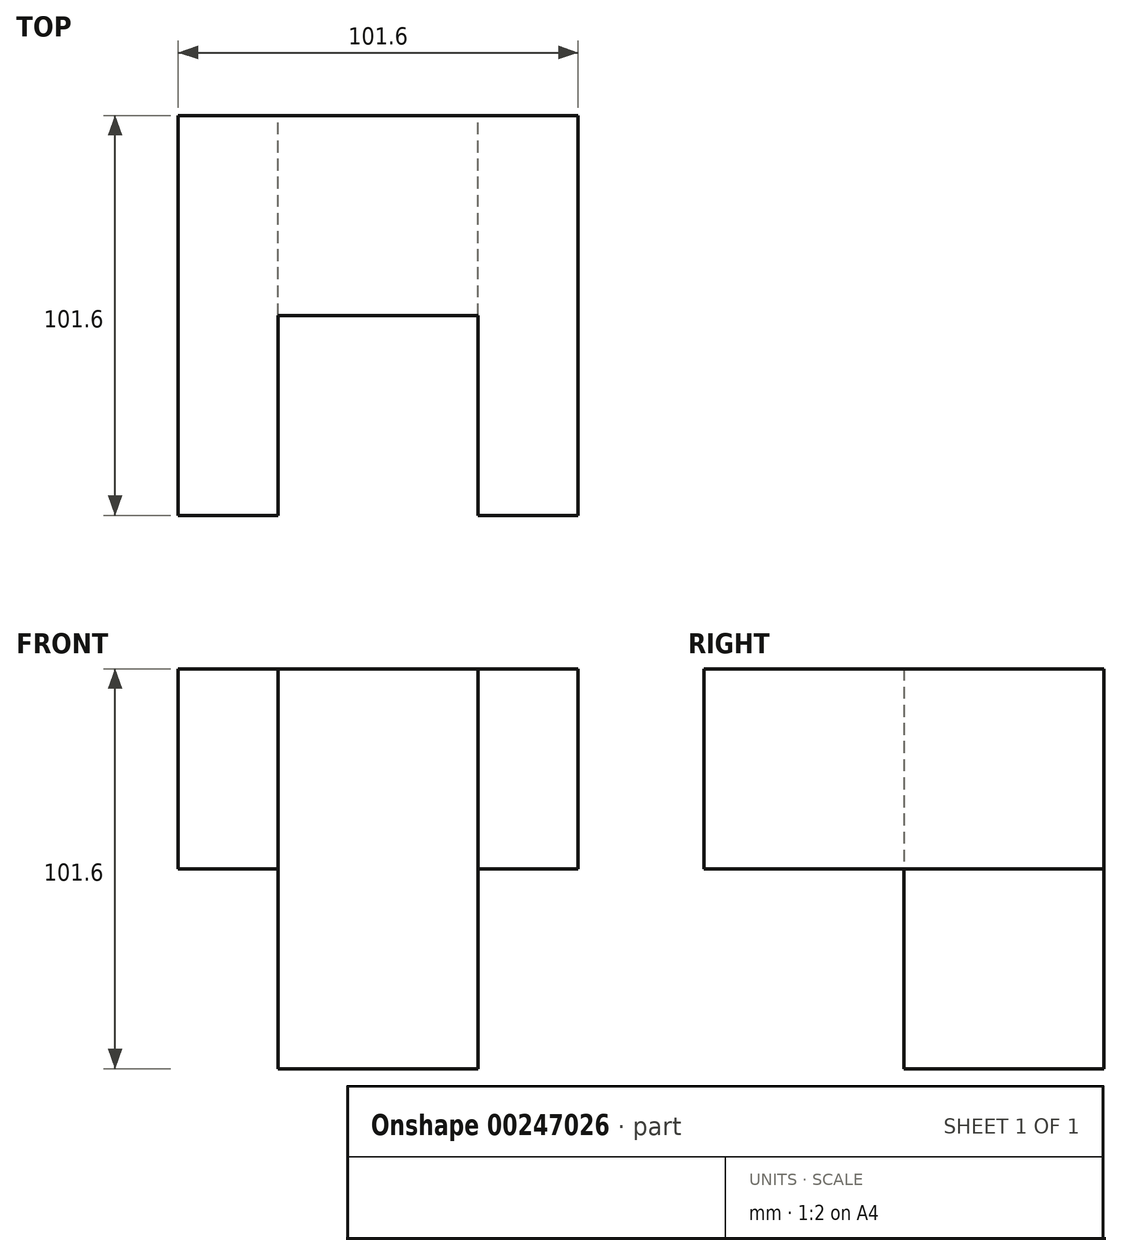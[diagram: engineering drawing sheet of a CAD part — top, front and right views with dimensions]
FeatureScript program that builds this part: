
annotation { "Feature Type Name" : "Feature", "Feature Type Description" : "" }
export const myFeature = defineFeature(function(context is Context, id is Id, definition is map)
    precondition{}
    {
        {
            var Q0;
            Q0=qCreatedBy(makeId("Front.planeOp"),FACE);
            var sketch = newSketch(context, id + "F0", { "sketchPlane" : qUnion([Q0])});
            skLineSegment(sketch, "E0.bottom", {"start": v(-58.42, 78.35) * mm, "end": v(43.18, 78.35) * mm});
            skLineSegment(sketch, "E0.top", {"start": v(-58.42, 27.55) * mm, "end": v(43.18, 27.55) * mm});
            skLineSegment(sketch, "E0.left", {"start": v(-58.42, 78.35) * mm, "end": v(-58.42, 27.55) * mm});
            skLineSegment(sketch, "E0.right", {"start": v(43.18, 78.35) * mm, "end": v(43.18, 27.55) * mm});
            skSolve(sketch);
        }
        {
            var Q0;
            Q0=makeQuery(id+"F0.imprint","IMPRINT",FACE,{"disambiguationData":[TD([[makeQuery(id+"F0.imprint","IMPRINT",EDGE,{"derivedFrom":sQuery(id+"F0.wireOp",EDGE,"E0.bottom")}),-1.0]])]});
            extrude(context, id + "F1", {"entities" : qUnion([Q0]), "depth" : 50.8 * mm});
        }
        {
            var Q0;
            Q0=makeQuery(id+"F1.opExtrude","SWEPT_FACE",FACE,{"disambiguationData":[OSD([sQuery(id+"F0.wireOp",EDGE,"E0.bottom")])]});
            var sketch = newSketch(context, id + "F2", { "sketchPlane" : qUnion([Q0])});
            skLineSegment(sketch, "E1.bottom", {"start": v(-58.42, 0) * mm, "end": v(-33.02, 0) * mm});
            skLineSegment(sketch, "E1.top", {"start": v(-58.42, -101.6) * mm, "end": v(-33.02, -101.6) * mm});
            skLineSegment(sketch, "E1.left", {"start": v(-58.42, 0) * mm, "end": v(-58.42, -101.6) * mm});
            skLineSegment(sketch, "E1.right", {"start": v(-33.02, 0) * mm, "end": v(-33.02, -101.6) * mm});
            skLineSegment(sketch, "E2.bottom", {"start": v(43.18, 0) * mm, "end": v(17.78, 0) * mm});
            skLineSegment(sketch, "E2.top", {"start": v(43.18, -101.6) * mm, "end": v(17.78, -101.6) * mm});
            skLineSegment(sketch, "E2.left", {"start": v(43.18, 0) * mm, "end": v(43.18, -101.6) * mm});
            skLineSegment(sketch, "E2.right", {"start": v(17.78, 0) * mm, "end": v(17.78, -101.6) * mm});
            skSolve(sketch);
        }
        {
            var Q0;
            Q0 = qSketchRegion(id + "F2", true);
            extrude(context, id + "F3", {"entities" : qUnion([Q0]), "operationType" : NewBodyOperationType.ADD, "oppositeDirection" : true, "depth" : 50.8 * mm});
        }
        {
            var Q0;
            Q0=makeQuery(id+"F3.boolean.opBoolean","MERGE",FACE,{"derivedFrom":[makeQuery(id+"F1.opExtrude","SWEPT_FACE",FACE,{"disambiguationData":[OSD([sQuery(id+"F0.wireOp",EDGE,"E0.top")])]}),makeQuery(id+"F3.opExtrude","CAP_FACE",FACE,{"disambiguationData":[OSD([sQuery(id+"F2.wireOp",EDGE,"E1.bottom"),sQuery(id+"F2.wireOp",EDGE,"E1.top"),sQuery(id+"F2.wireOp",EDGE,"E1.left"),sQuery(id+"F2.wireOp",EDGE,"E1.right")])],"isStart":false}),makeQuery(id+"F3.opExtrude","CAP_FACE",FACE,{"disambiguationData":[OSD([sQuery(id+"F2.wireOp",EDGE,"E2.bottom"),sQuery(id+"F2.wireOp",EDGE,"E2.top"),sQuery(id+"F2.wireOp",EDGE,"E2.left"),sQuery(id+"F2.wireOp",EDGE,"E2.right")])],"isStart":false})]});
            var sketch = newSketch(context, id + "F4", { "sketchPlane" : qUnion([Q0])});
            skLineSegment(sketch, "E3.bottom", {"start": v(-33.02, 50.8) * mm, "end": v(17.78, 50.8) * mm});
            skLineSegment(sketch, "E3.top", {"start": v(-33.02, 0) * mm, "end": v(17.78, 0) * mm});
            skLineSegment(sketch, "E3.left", {"start": v(-33.02, 50.8) * mm, "end": v(-33.02, 0) * mm});
            skLineSegment(sketch, "E3.right", {"start": v(17.78, 50.8) * mm, "end": v(17.78, 0) * mm});
            skSolve(sketch);
        }
        {
            var Q0;
            Q0=makeQuery(id+"F4.imprint","IMPRINT",FACE,{"disambiguationData":[TD([[makeQuery(id+"F4.imprint","IMPRINT",EDGE,{"derivedFrom":sQuery(id+"F4.wireOp",EDGE,"E3.bottom")}),-1.0]])]});
            extrude(context, id + "F5", {"entities" : qUnion([Q0]), "operationType" : NewBodyOperationType.ADD, "depth" : 50.8 * mm});
        }
    });
